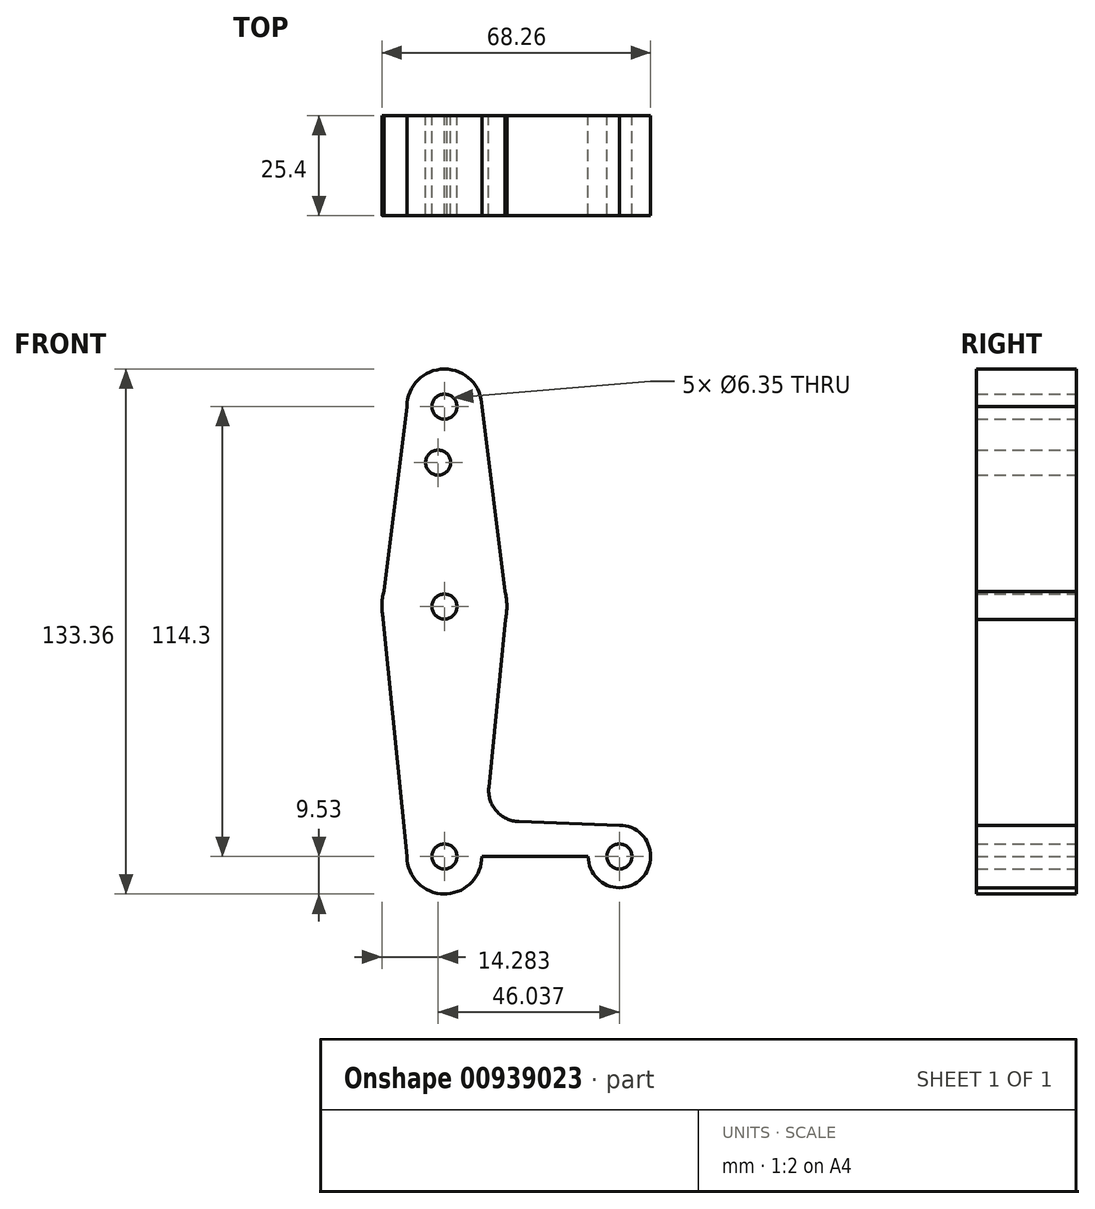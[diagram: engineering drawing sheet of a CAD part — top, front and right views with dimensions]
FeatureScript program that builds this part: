
annotation { "Feature Type Name" : "Feature", "Feature Type Description" : "" }
export const myFeature = defineFeature(function(context is Context, id is Id, definition is map)
    precondition{}
    {
        {
            var Q0;
            Q0=qCreatedBy(makeId("Front.planeOp"),FACE);
            var sketch = newSketch(context, id + "F0", { "sketchPlane" : qUnion([Q0])});
            skCircle(sketch, "E0", {"center": v(0, 114.3) * mm, "radius": 9.53 * mm});
            skCircle(sketch, "E1", {"center": v(0, 63.5) * mm, "radius": 15.88 * mm});
            skCircle(sketch, "E2", {"center": v(0, 0) * mm, "radius": 9.53 * mm});
            skLineSegment(sketch, "E3", {"start": v(0, 0) * mm, "end": v(44.45, 0) * mm});
            skCircle(sketch, "E4", {"center": v(44.45, 0) * mm, "radius": 7.94 * mm});
            skLineSegment(sketch, "E5", {"start": v(0, 63.5) * mm, "end": v(0, 0) * mm});
            skLineSegment(sketch, "E6", {"start": v(0, 114.3) * mm, "end": v(0, 63.5) * mm});
            skLineSegment(sketch, "E7", {"start": v(9.52, 114.3) * mm, "end": v(15.87, 63.64) * mm});
            skLineSegment(sketch, "E8", {"start": v(-15.87, 63.5) * mm, "end": v(-9.53, 114.3) * mm});
            skLineSegment(sketch, "E9", {"start": v(-15.87, 63.5) * mm, "end": v(-9.53, 0) * mm});
            skLineSegment(sketch, "E10", {"start": v(15.87, 63.64) * mm, "end": v(11.28, 17.58) * mm});
            skLineSegment(sketch, "E11", {"start": v(18.9, 8.85) * mm, "end": v(44.45, 7.94) * mm});
            skLineSegment(sketch, "E12", {"start": v(0, -9.52) * mm, "end": v(44.45, -7.94) * mm});
            skCircle(sketch, "E13.1.0.0", {"center": v(-1.59, 100.07) * mm, "radius": 3.18 * mm});
            skLineSegment(sketch, "E13.direction1", {"start": v(0, 100.03) * mm, "end": v(-1.59, 100.07) * mm, "construction": true});
            skCircle(sketch, "E14", {"center": v(0, 63.5) * mm, "radius": 3.18 * mm});
            skCircle(sketch, "E15", {"center": v(0, 114.3) * mm, "radius": 3.18 * mm});
            skCircle(sketch, "E16", {"center": v(44.45, 0) * mm, "radius": 3.18 * mm});
            skCircle(sketch, "E17", {"center": v(0, 0) * mm, "radius": 3.18 * mm});
            skArc(sketch, "E18.filletArc", {"start": v(11.28, 17.58) * mm, "mid": v(13.2, 11.57) * mm, "end": v(18.9, 8.85) * mm});
            skSolve(sketch);
        }
        {
            var Q0;
            {var subQ0=sQuery(id+"F0.wireOp",EDGE,"E7");var subQ1=sQuery(id+"F0.wireOp",EDGE,"E1");var subQ3=makeQuery(id+"F0.imprint","INTERSECT",VERTEX,{"derivedFrom":[subQ1,subQ0]});Q0=makeQuery(id+"F0.imprint","IMPRINT",FACE,{"disambiguationData":[TD([[makeQuery(id+"F0.imprint","IMPRINT",EDGE,{"disambiguationData":[TD([[subQ3,1.0]])],"derivedFrom":subQ1}),1.0]])]});}
            var Q1;
            {var subQ0=sQuery(id+"F0.wireOp",EDGE,"E8");var subQ1=sQuery(id+"F0.wireOp",EDGE,"E1");var subQ3=makeQuery(id+"F0.imprint","INTERSECT",VERTEX,{"derivedFrom":[subQ1,subQ0]});Q1=makeQuery(id+"F0.imprint","IMPRINT",FACE,{"disambiguationData":[TD([[makeQuery(id+"F0.imprint","IMPRINT",EDGE,{"disambiguationData":[TD([[subQ3,-1.0]])],"derivedFrom":subQ1}),1.0]])]});}
            var Q2;
            {var subQ0=sQuery(id+"F0.wireOp",EDGE,"E9");var subQ1=sQuery(id+"F0.wireOp",EDGE,"E1");var subQ3=makeQuery(id+"F0.imprint","INTERSECT",VERTEX,{"derivedFrom":[subQ1,subQ0]});Q2=makeQuery(id+"F0.imprint","IMPRINT",FACE,{"disambiguationData":[TD([[makeQuery(id+"F0.imprint","IMPRINT",EDGE,{"disambiguationData":[TD([[subQ3,1.0]])],"derivedFrom":subQ1}),1.0]])]});}
            var Q3;
            {var subQ0=sQuery(id+"F0.wireOp",EDGE,"E10");var subQ1=sQuery(id+"F0.wireOp",EDGE,"E1");var subQ3=makeQuery(id+"F0.imprint","INTERSECT",VERTEX,{"derivedFrom":[subQ1,subQ0]});Q3=makeQuery(id+"F0.imprint","IMPRINT",FACE,{"disambiguationData":[TD([[makeQuery(id+"F0.imprint","IMPRINT",EDGE,{"disambiguationData":[TD([[subQ3,-1.0]])],"derivedFrom":subQ1}),1.0]])]});}
            var Q4;
            {var subQ0=sQuery(id+"F0.wireOp",EDGE,"E12");var subQ1=sQuery(id+"F0.wireOp",EDGE,"E2");var subQ2=makeQuery(id+"F0.imprint","INTERSECT",VERTEX,{"disambiguationData":[OD(0.0)],"derivedFrom":[subQ1,subQ0]});Q4=makeQuery(id+"F0.imprint","IMPRINT",FACE,{"disambiguationData":[TD([[makeQuery(id+"F0.imprint","IMPRINT",EDGE,{"disambiguationData":[TD([[subQ2,-1.0]])],"derivedFrom":subQ1}),1.0]])]});}
            var Q5;
            Q5=makeQuery(id+"F0.imprint","IMPRINT",FACE,{"disambiguationData":[TD([[makeQuery(id+"F0.imprint","IMPRINT",EDGE,{"derivedFrom":sQuery(id+"F0.wireOp",EDGE,"E15")}),-1.0]])]});
            var Q6;
            {var subQ0=sQuery(id+"F0.wireOp",EDGE,"E9");var subQ1=sQuery(id+"F0.wireOp",EDGE,"E1");var subQ2=makeQuery(id+"F0.imprint","INTERSECT",VERTEX,{"derivedFrom":[subQ1,subQ0]});Q6=makeQuery(id+"F0.imprint","IMPRINT",FACE,{"disambiguationData":[TD([[makeQuery(id+"F0.imprint","IMPRINT",EDGE,{"disambiguationData":[TD([[subQ2,-1.0]])],"derivedFrom":subQ1}),-1.0]])]});}
            var Q7;
            {var subQ0=sQuery(id+"F0.wireOp",EDGE,"E12");var subQ1=sQuery(id+"F0.wireOp",EDGE,"E2");var subQ2=makeQuery(id+"F0.imprint","INTERSECT",VERTEX,{"disambiguationData":[OD(1.0)],"derivedFrom":[subQ1,subQ0]});Q7=makeQuery(id+"F0.imprint","IMPRINT",FACE,{"disambiguationData":[TD([[makeQuery(id+"F0.imprint","IMPRINT",EDGE,{"disambiguationData":[TD([[subQ2,-1.0]])],"derivedFrom":subQ1}),-1.0]])]});}
            var Q8;
            Q8=makeQuery(id+"F0.imprint","IMPRINT",FACE,{"disambiguationData":[TD([[makeQuery(id+"F0.imprint","IMPRINT",EDGE,{"derivedFrom":sQuery(id+"F0.wireOp",EDGE,"E16")}),-1.0]])]});
            var Q9;
            {var subQ5=sQuery(id+"F0.wireOp",EDGE,"E7");var subQ7=sQuery(id+"F0.wireOp",EDGE,"E0");var subQ10=makeQuery(id+"F0.imprint","INTERSECT",VERTEX,{"derivedFrom":[subQ7,subQ5]});Q9=makeQuery(id+"F0.imprint","IMPRINT",FACE,{"disambiguationData":[TD([[makeQuery(id+"F0.imprint","IMPRINT",EDGE,{"disambiguationData":[TD([[subQ10,1.0]])],"derivedFrom":subQ7}),-1.0]])]});}
            var Q10;
            {var subQ5=sQuery(id+"F0.wireOp",EDGE,"E11");Q10=makeQuery(id+"F0.imprint","IMPRINT",FACE,{"disambiguationData":[TD([[makeQuery(id+"F0.imprint","IMPRINT",EDGE,{"derivedFrom":subQ5}),-1.0]])]});}
            var Q11;
            {var subQ1=sQuery(id+"F0.wireOp",EDGE,"E2");var subQ5=makeQuery(id+"F0.imprint","INTERSECT",VERTEX,{"derivedFrom":[subQ1,sQuery(id+"F0.wireOp",EDGE,"E9")]});Q11=makeQuery(id+"F0.imprint","IMPRINT",FACE,{"disambiguationData":[TD([[makeQuery(id+"F0.imprint","IMPRINT",EDGE,{"disambiguationData":[TD([[subQ5,1.0]])],"derivedFrom":subQ1}),1.0]])]});}
            var Q12;
            {var subQ1=sQuery(id+"F0.wireOp",EDGE,"E1");var subQ10=sQuery(id+"F0.wireOp",EDGE,"E7");var subQ11=makeQuery(id+"F0.imprint","INTERSECT",VERTEX,{"derivedFrom":[subQ1,subQ10]});Q12=makeQuery(id+"F0.imprint","IMPRINT",FACE,{"disambiguationData":[TD([[makeQuery(id+"F0.imprint","IMPRINT",EDGE,{"disambiguationData":[TD([[subQ11,-1.0]])],"derivedFrom":subQ1}),1.0]])]});}
            var Q13;
            {var subQ1=sQuery(id+"F0.wireOp",EDGE,"E1");var subQ6=sQuery(id+"F0.wireOp",EDGE,"E8");var subQ8=makeQuery(id+"F0.imprint","INTERSECT",VERTEX,{"derivedFrom":[subQ1,subQ6]});Q13=makeQuery(id+"F0.imprint","IMPRINT",FACE,{"disambiguationData":[TD([[makeQuery(id+"F0.imprint","IMPRINT",EDGE,{"disambiguationData":[TD([[subQ8,1.0]])],"derivedFrom":subQ1}),1.0]])]});}
            var Q14;
            {var subQ5=sQuery(id+"F0.wireOp",EDGE,"E0");var subQ8=sQuery(id+"F0.wireOp",EDGE,"E8");var subQ10=makeQuery(id+"F0.imprint","INTERSECT",VERTEX,{"derivedFrom":[subQ5,subQ8]});Q14=makeQuery(id+"F0.imprint","IMPRINT",FACE,{"disambiguationData":[TD([[makeQuery(id+"F0.imprint","IMPRINT",EDGE,{"disambiguationData":[TD([[subQ10,-1.0]])],"derivedFrom":subQ5}),-1.0]])]});}
            var Q15;
            {var subQ0=sQuery(id+"F0.wireOp",EDGE,"E5");var subQ1=sQuery(id+"F0.wireOp",EDGE,"E2");var subQ2=makeQuery(id+"F0.imprint","INTERSECT",VERTEX,{"derivedFrom":[subQ1,subQ0]});Q15=makeQuery(id+"F0.imprint","IMPRINT",FACE,{"disambiguationData":[TD([[makeQuery(id+"F0.imprint","IMPRINT",EDGE,{"disambiguationData":[TD([[subQ2,1.0]])],"derivedFrom":subQ1}),1.0]])]});}
            extrude(context, id + "F1", {"entities" : qUnion([Q0, Q1, Q2, Q3, Q4, Q5, Q6, Q7, Q8, Q9, Q10, Q11, Q12, Q13, Q14, Q15]), "depth" : 25.4 * mm, "offsetDistance" : 25.4 * mm});
        }
    });
